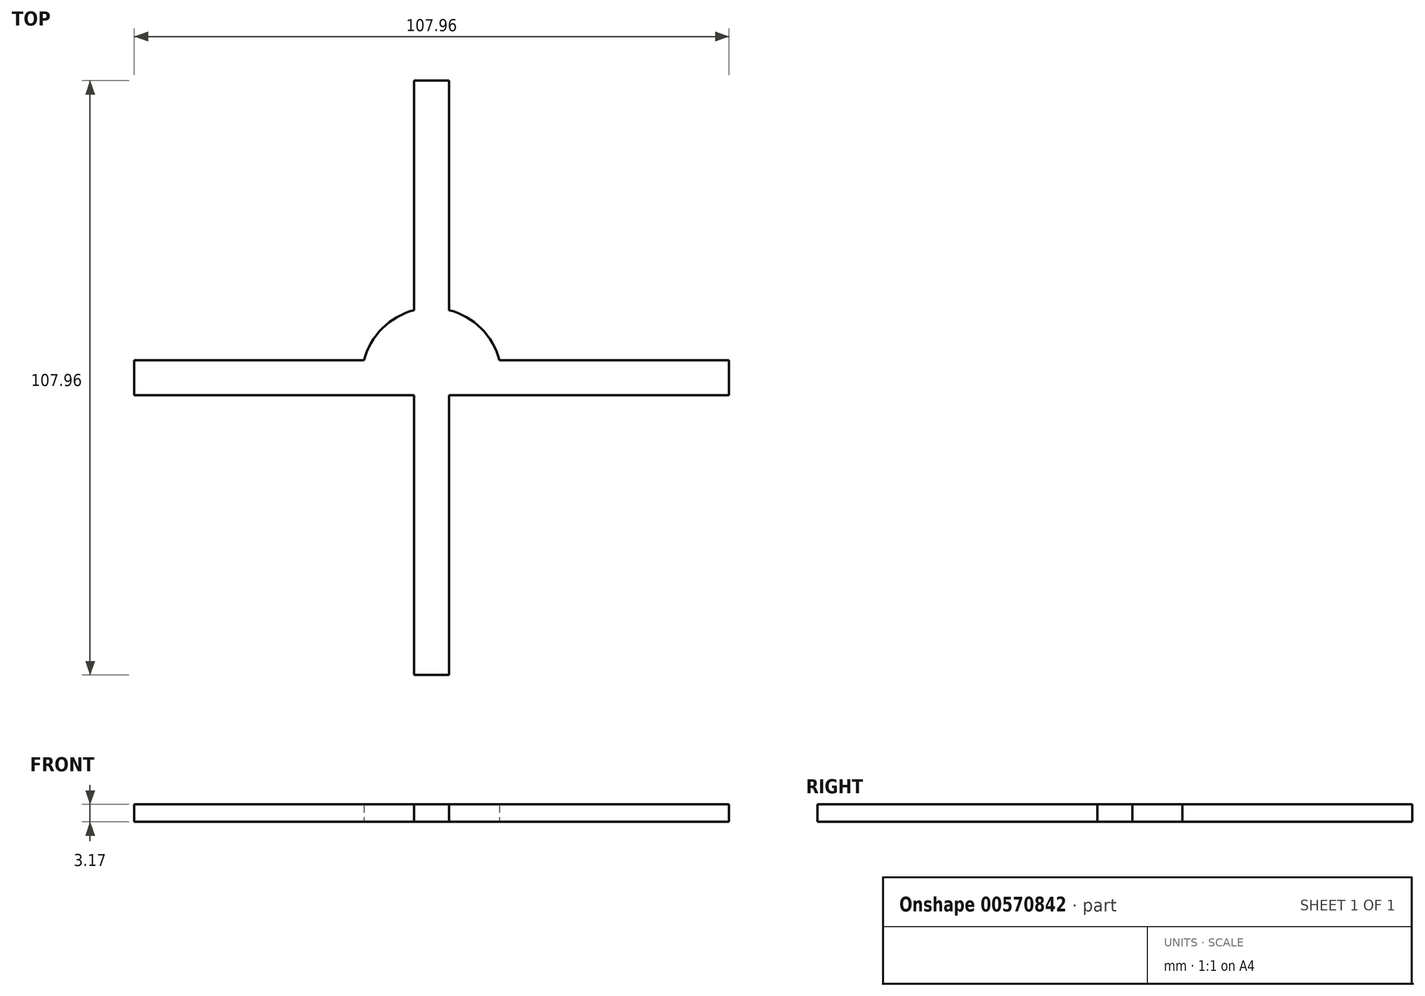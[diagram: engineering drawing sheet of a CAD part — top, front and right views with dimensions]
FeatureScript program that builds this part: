
annotation { "Feature Type Name" : "Feature", "Feature Type Description" : "" }
export const myFeature = defineFeature(function(context is Context, id is Id, definition is map)
    precondition{}
    {
        {
            var Q0;
            Q0=qCreatedBy(makeId("Top.planeOp"),FACE);
            var sketch = newSketch(context, id + "F0", { "sketchPlane" : qUnion([Q0])});
            skLineSegment(sketch, "E0.bottom", {"start": v(-53.98, 3.17) * mm, "end": v(53.98, 3.17) * mm});
            skLineSegment(sketch, "E0.top", {"start": v(-53.98, -3.18) * mm, "end": v(53.98, -3.18) * mm});
            skLineSegment(sketch, "E0.left", {"start": v(-53.98, 3.17) * mm, "end": v(-53.98, -3.18) * mm});
            skLineSegment(sketch, "E0.right", {"start": v(53.98, 3.17) * mm, "end": v(53.98, -3.17) * mm});
            skPoint(sketch, "E0.middle", {"position": v(0, 0) * mm});
            skLineSegment(sketch, "E1.bottom", {"start": v(-3.18, 53.98) * mm, "end": v(3.17, 53.98) * mm});
            skLineSegment(sketch, "E1.top", {"start": v(-3.17, -53.98) * mm, "end": v(3.18, -53.98) * mm});
            skLineSegment(sketch, "E1.left", {"start": v(-3.18, 53.98) * mm, "end": v(-3.17, -53.98) * mm});
            skLineSegment(sketch, "E1.right", {"start": v(3.17, 53.98) * mm, "end": v(3.18, -53.98) * mm});
            skCircle(sketch, "E2", {"center": v(0, 0) * mm, "radius": 12.7 * mm});
            skSolve(sketch);
        }
        {
            var Q0;
            {var subQ0=sQuery(id+"F0.wireOp",EDGE,"E0.left");Q0=makeQuery(id+"F0.imprint","IMPRINT",FACE,{"disambiguationData":[TD([[makeQuery(id+"F0.imprint","IMPRINT",EDGE,{"derivedFrom":subQ0}),1.0]])]});}
            var Q1;
            {var subQ0=sQuery(id+"F0.wireOp",EDGE,"E0.right");Q1=makeQuery(id+"F0.imprint","IMPRINT",FACE,{"disambiguationData":[TD([[makeQuery(id+"F0.imprint","IMPRINT",EDGE,{"derivedFrom":subQ0}),-1.0]])]});}
            var Q2;
            {var subQ0=sQuery(id+"F0.wireOp",EDGE,"E1.top");Q2=makeQuery(id+"F0.imprint","IMPRINT",FACE,{"disambiguationData":[TD([[makeQuery(id+"F0.imprint","IMPRINT",EDGE,{"derivedFrom":subQ0}),1.0]])]});}
            var Q3;
            {var subQ0=sQuery(id+"F0.wireOp",EDGE,"E1.bottom");Q3=makeQuery(id+"F0.imprint","IMPRINT",FACE,{"disambiguationData":[TD([[makeQuery(id+"F0.imprint","IMPRINT",EDGE,{"derivedFrom":subQ0}),-1.0]])]});}
            var Q4;
            {var subQ0=sQuery(id+"F0.wireOp",EDGE,"E2");var subQ1=sQuery(id+"F0.wireOp",EDGE,"E0.bottom");var subQ2=makeQuery(id+"F0.imprint","INTERSECT",VERTEX,{"disambiguationData":[OD(0.0)],"derivedFrom":[subQ1,subQ0]});Q4=makeQuery(id+"F0.imprint","IMPRINT",FACE,{"disambiguationData":[TD([[makeQuery(id+"F0.imprint","IMPRINT",EDGE,{"disambiguationData":[TD([[subQ2,-1.0]])],"derivedFrom":subQ1}),1.0]])]});}
            var Q5;
            {var subQ0=sQuery(id+"F0.wireOp",EDGE,"E2");var subQ1=sQuery(id+"F0.wireOp",EDGE,"E0.bottom");var subQ2=makeQuery(id+"F0.imprint","INTERSECT",VERTEX,{"disambiguationData":[OD(1.0)],"derivedFrom":[subQ1,subQ0]});Q5=makeQuery(id+"F0.imprint","IMPRINT",FACE,{"disambiguationData":[TD([[makeQuery(id+"F0.imprint","IMPRINT",EDGE,{"disambiguationData":[TD([[subQ2,1.0]])],"derivedFrom":subQ1}),1.0]])]});}
            var Q6;
            {var subQ0=sQuery(id+"F0.wireOp",EDGE,"E2");var subQ1=sQuery(id+"F0.wireOp",EDGE,"E0.top");var subQ2=makeQuery(id+"F0.imprint","INTERSECT",VERTEX,{"disambiguationData":[OD(0.0)],"derivedFrom":[subQ1,subQ0]});Q6=makeQuery(id+"F0.imprint","IMPRINT",FACE,{"disambiguationData":[TD([[makeQuery(id+"F0.imprint","IMPRINT",EDGE,{"disambiguationData":[TD([[subQ2,-1.0]])],"derivedFrom":subQ1}),-1.0]])]});}
            var Q7;
            {var subQ0=sQuery(id+"F0.wireOp",EDGE,"E2");var subQ1=sQuery(id+"F0.wireOp",EDGE,"E0.top");var subQ2=makeQuery(id+"F0.imprint","INTERSECT",VERTEX,{"disambiguationData":[OD(1.0)],"derivedFrom":[subQ1,subQ0]});Q7=makeQuery(id+"F0.imprint","IMPRINT",FACE,{"disambiguationData":[TD([[makeQuery(id+"F0.imprint","IMPRINT",EDGE,{"disambiguationData":[TD([[subQ2,1.0]])],"derivedFrom":subQ1}),-1.0]])]});}
            var Q8;
            {var subQ0=sQuery(id+"F0.wireOp",EDGE,"E2");var subQ1=sQuery(id+"F0.wireOp",EDGE,"E0.bottom");var subQ2=makeQuery(id+"F0.imprint","INTERSECT",VERTEX,{"disambiguationData":[OD(0.0)],"derivedFrom":[subQ1,subQ0]});Q8=makeQuery(id+"F0.imprint","IMPRINT",FACE,{"disambiguationData":[TD([[makeQuery(id+"F0.imprint","IMPRINT",EDGE,{"disambiguationData":[TD([[subQ2,-1.0]])],"derivedFrom":subQ1}),-1.0]])]});}
            var Q9;
            {var subQ0=sQuery(id+"F0.wireOp",EDGE,"E1.left");var subQ1=sQuery(id+"F0.wireOp",EDGE,"E0.bottom");var subQ2=makeQuery(id+"F0.imprint","INTERSECT",VERTEX,{"derivedFrom":[subQ1,subQ0]});Q9=makeQuery(id+"F0.imprint","IMPRINT",FACE,{"disambiguationData":[TD([[makeQuery(id+"F0.imprint","IMPRINT",EDGE,{"disambiguationData":[TD([[subQ2,-1.0]])],"derivedFrom":subQ1}),1.0]])]});}
            var Q10;
            {var subQ0=sQuery(id+"F0.wireOp",EDGE,"E2");var subQ1=sQuery(id+"F0.wireOp",EDGE,"E0.bottom");var subQ2=makeQuery(id+"F0.imprint","INTERSECT",VERTEX,{"disambiguationData":[OD(1.0)],"derivedFrom":[subQ1,subQ0]});Q10=makeQuery(id+"F0.imprint","IMPRINT",FACE,{"disambiguationData":[TD([[makeQuery(id+"F0.imprint","IMPRINT",EDGE,{"disambiguationData":[TD([[subQ2,1.0]])],"derivedFrom":subQ1}),-1.0]])]});}
            var Q11;
            {var subQ0=sQuery(id+"F0.wireOp",EDGE,"E1.left");var subQ1=sQuery(id+"F0.wireOp",EDGE,"E0.top");var subQ2=makeQuery(id+"F0.imprint","INTERSECT",VERTEX,{"derivedFrom":[subQ1,subQ0]});Q11=makeQuery(id+"F0.imprint","IMPRINT",FACE,{"disambiguationData":[TD([[makeQuery(id+"F0.imprint","IMPRINT",EDGE,{"disambiguationData":[TD([[subQ2,-1.0]])],"derivedFrom":subQ1}),-1.0]])]});}
            var Q12;
            {var subQ0=sQuery(id+"F0.wireOp",EDGE,"E1.left");var subQ1=sQuery(id+"F0.wireOp",EDGE,"E0.bottom");var subQ2=makeQuery(id+"F0.imprint","INTERSECT",VERTEX,{"derivedFrom":[subQ1,subQ0]});Q12=makeQuery(id+"F0.imprint","IMPRINT",FACE,{"disambiguationData":[TD([[makeQuery(id+"F0.imprint","IMPRINT",EDGE,{"disambiguationData":[TD([[subQ2,-1.0]])],"derivedFrom":subQ1}),-1.0]])]});}
            extrude(context, id + "F1", {"entities" : qUnion([Q0, Q1, Q2, Q3, Q4, Q5, Q6, Q7, Q8, Q9, Q10, Q11, Q12]), "depth" : 3.17 * mm, "offsetDistance" : 25 * mm});
        }
    });
